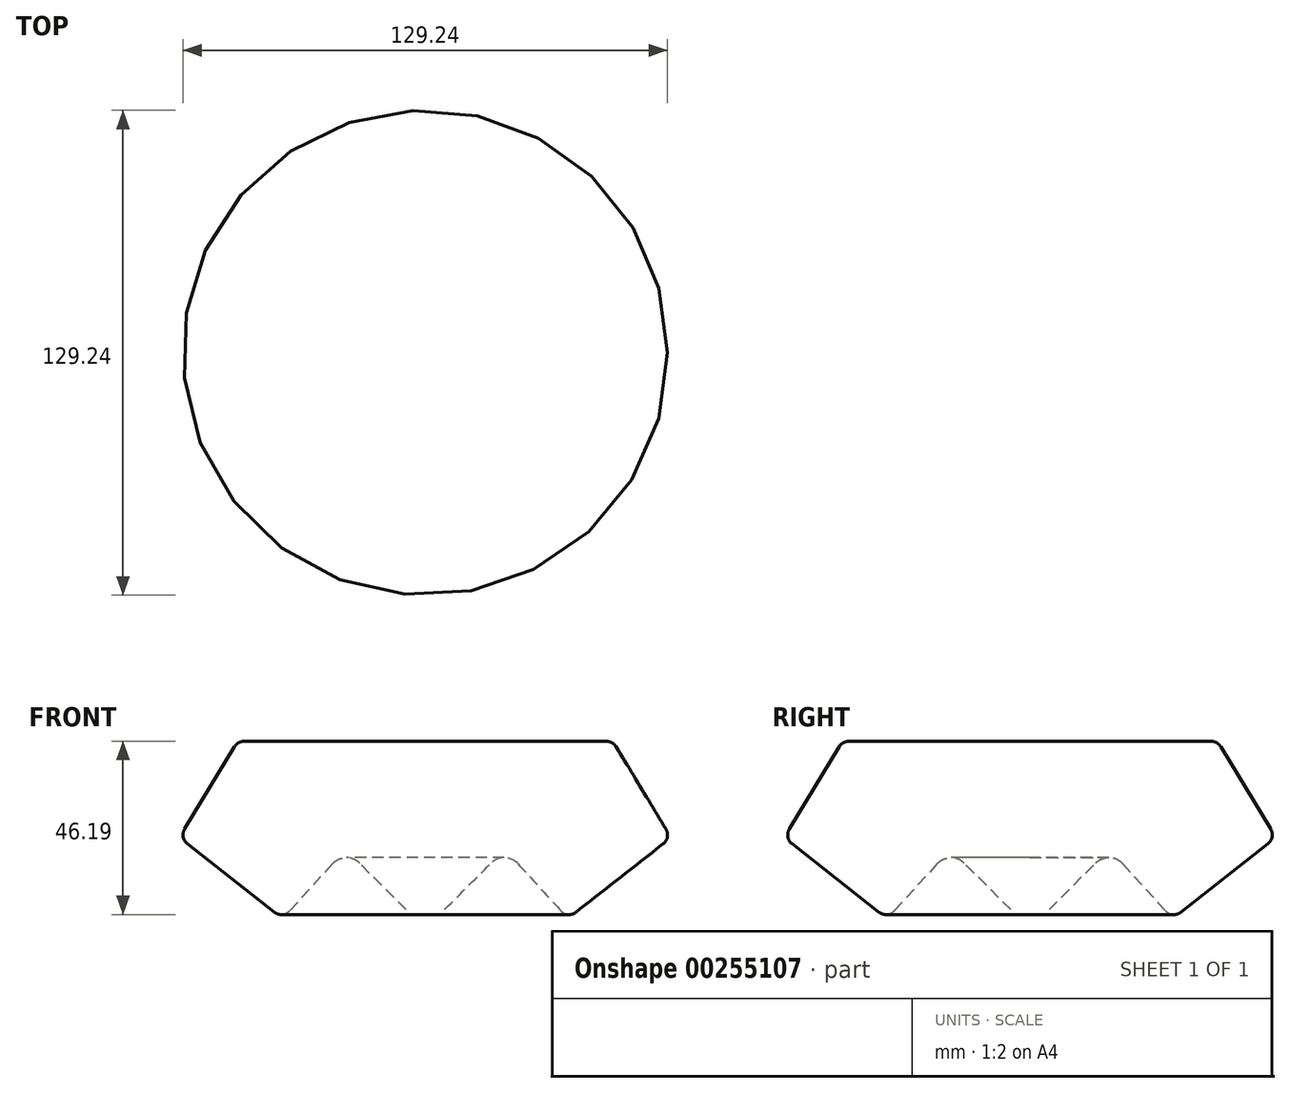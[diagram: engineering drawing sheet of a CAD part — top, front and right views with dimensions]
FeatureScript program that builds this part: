
annotation { "Feature Type Name" : "Feature", "Feature Type Description" : "" }
export const myFeature = defineFeature(function(context is Context, id is Id, definition is map)
    precondition{}
    {
        {
            var Q0;
            Q0=qCreatedBy(makeId("Front.planeOp"),FACE);
            var sketch = newSketch(context, id + "F0", { "sketchPlane" : qUnion([Q0])});
            skLineSegment(sketch, "E0", {"start": v(0, -42.76) * mm, "end": v(0, 0) * mm});
            skLineSegment(sketch, "E1", {"start": v(0, 0) * mm, "end": v(48.31, 0) * mm});
            skLineSegment(sketch, "E2", {"start": v(50.88, -1.44) * mm, "end": v(64.18, -23.38) * mm});
            skLineSegment(sketch, "E3", {"start": v(63.47, -27.3) * mm, "end": v(40.23, -45.55) * mm});
            skLineSegment(sketch, "E4", {"start": v(36.16, -45.21) * mm, "end": v(24.74, -32.66) * mm});
            skLineSegment(sketch, "E5", {"start": v(17.5, -32.5) * mm, "end": v(5.12, -44.88) * mm});
            skPoint(sketch, "E6.visualSharp", {"position": v(50, 0) * mm});
            skArc(sketch, "E6.filletArc", {"start": v(50.88, -1.44) * mm, "mid": v(49.78, -0.39) * mm, "end": v(48.31, 0) * mm});
            skPoint(sketch, "E7.visualSharp", {"position": v(0, -50) * mm});
            skArc(sketch, "E7.filletArc", {"start": v(0, -42.76) * mm, "mid": v(1.85, -45.53) * mm, "end": v(5.12, -44.88) * mm});
            skPoint(sketch, "E8.visualSharp", {"position": v(38.04, -47.28) * mm});
            skArc(sketch, "E8.filletArc", {"start": v(36.16, -45.21) * mm, "mid": v(38.13, -46.18) * mm, "end": v(40.23, -45.55) * mm});
            skPoint(sketch, "E9.visualSharp", {"position": v(65.56, -25.65) * mm});
            skArc(sketch, "E9.filletArc", {"start": v(63.47, -27.3) * mm, "mid": v(64.57, -25.47) * mm, "end": v(64.18, -23.38) * mm});
            skPoint(sketch, "E10.visualSharp", {"position": v(21.21, -28.79) * mm});
            skArc(sketch, "E10.filletArc", {"start": v(24.74, -32.66) * mm, "mid": v(21.16, -31.03) * mm, "end": v(17.5, -32.5) * mm});
            skLineSegment(sketch, "E11", {"start": v(0, 54.08) * mm, "end": v(0, -63.55) * mm, "construction": true});
            skSolve(sketch);
        }
        {
            var Q0;
            Q0=makeQuery(id+"F0.imprint","IMPRINT",FACE,{"disambiguationData":[TD([[makeQuery(id+"F0.imprint","IMPRINT",EDGE,{"derivedFrom":sQuery(id+"F0.wireOp",EDGE,"E0")}),-1.0]])]});
            var Q1;
            Q1=sQuery(id+"F0.wireOp",EDGE,"E11");
            revolve(context, id + "F1", {"entities" : qUnion([Q0]), "axis" : qUnion([Q1]), "revolveType" : RevolveType.FULL});
        }
    });
